# Revit family: 1Electronics_Commercial-Audio_Biamp_Volume-Control_E-VOLST
name_source: partatom
category: Communication Devices
units: mm (PartAtom-declared; Revit-internal decimal feet)

## family parameters
Cut with Voids When Loaded = No
Host = Face
Maintain Annotation Orientation = No
OmniClass Number = 23.85.10.11.14
OmniClass Title = Audio Equipment
Part Type = Normal
Room Calculation Point = No
Round Connector Dimension = Use Diameter
Shared = No

## types (1)
- E-VOLST
    Default Elevation = 4' - 0"
    Depth = 0' - 2 1/2"
    Description = E-VOLST Stereo, 2 x 40 Watts Euro Volume Control, White
    Height = 0' - 3"
    Housing Material = Biamp - Plastic - White
    Impedance in ohms = 4 - 8 - 16
    Manufacturer = Biamp
    Model = E-VOLST
    Mounting = Screw
    Product Documentation Link = https://downloads.biamp.com
    Product Page URL = https://www.biamp.com
    Product data url = https://www.bimobject.com
    Steps = 0 + 11
    Stereo/mono = Stereo
    URL = https://www.biamp.com
    Weight = 0.595 lb
    Width = 0' - 3"

## geometry (parser evidence)
native form markers: Sweep x2
no freeform markers — native parametric forms only
